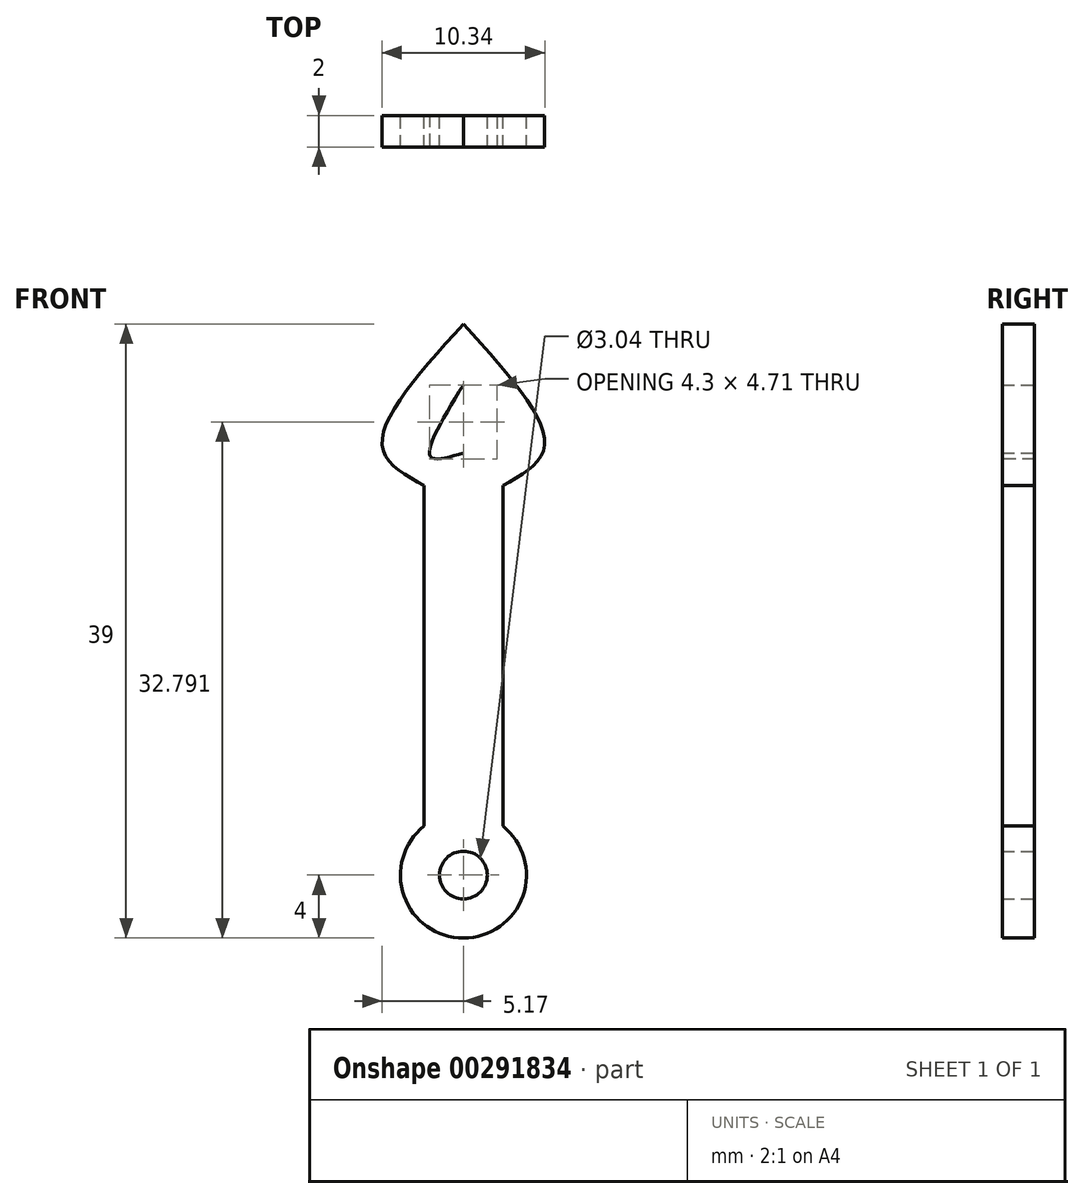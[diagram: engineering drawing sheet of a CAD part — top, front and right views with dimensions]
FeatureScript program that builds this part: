
annotation { "Feature Type Name" : "Feature", "Feature Type Description" : "" }
export const myFeature = defineFeature(function(context is Context, id is Id, definition is map)
    precondition{}
    {
        {
            var Q0;
            Q0=qCreatedBy(makeId("Front.planeOp"),FACE);
            var sketch = newSketch(context, id + "F0", { "sketchPlane" : qUnion([Q0])});
            skLineSegment(sketch, "E0.right", {"start": v(-2.5, 3.12) * mm, "end": v(-2.5, 24.74) * mm});
            skArc(sketch, "E1", {"start": v(-2.5, 3.12) * mm, "mid": v(-3.77, -1.32) * mm, "end": v(0, -4) * mm});
            skFitSpline(sketch, "E2", {"points": [v(0, 35) * mm, v(-5.16, 27.28) * mm, v(-2.5, 24.74) * mm], "startDerivative": vector(-13.09, -14.43) * mm, "endDerivative": vector(9.83, -5.4) * mm});
            skArc(sketch, "E3", {"start": v(0, 1.52) * mm, "mid": v(-1.52, 0) * mm, "end": v(0, -1.52) * mm});
            skFitSpline(sketch, "E4", {"points": [v(0, 31.14) * mm, v(-2.1, 26.59) * mm, v(0, 26.82) * mm], "startDerivative": vector(-6.1, -9.96) * mm, "endDerivative": vector(7.04, 2.18) * mm});
            skLineSegment(sketch, "E5.MirrorCS", {"start": v(2.5, 3.12) * mm, "end": v(2.5, 24.74) * mm});
            skFitSpline(sketch, "E6.MirrorCS", {"points": [v(0, 35) * mm, v(5.16, 27.28) * mm, v(2.5, 24.74) * mm], "startDerivative": vector(13.09, -14.43) * mm, "endDerivative": vector(-9.83, -5.4) * mm});
            skFitSpline(sketch, "E7.MirrorCS", {"points": [v(0, 31.14) * mm, v(2.1, 26.59) * mm, v(0, 26.82) * mm], "startDerivative": vector(6.1, -9.96) * mm, "endDerivative": vector(-7.04, 2.18) * mm});
            skArc(sketch, "E8.MirrorCS", {"start": v(0, 1.52) * mm, "mid": v(1.52, 0) * mm, "end": v(0, -1.52) * mm});
            skArc(sketch, "E9.MirrorCS", {"start": v(2.5, 3.12) * mm, "mid": v(3.77, -1.32) * mm, "end": v(0, -4) * mm});
            skSolve(sketch);
        }
        {
            var Q0;
            Q0=makeQuery(id+"F0.imprint","IMPRINT",FACE,{"disambiguationData":[TD([[makeQuery(id+"F0.imprint","IMPRINT",EDGE,{"derivedFrom":sQuery(id+"F0.wireOp",EDGE,"E0.right")}),-1.0]])]});
            extrude(context, id + "F1", {"entities" : qUnion([Q0]), "depth" : 2 * mm});
        }
    });
